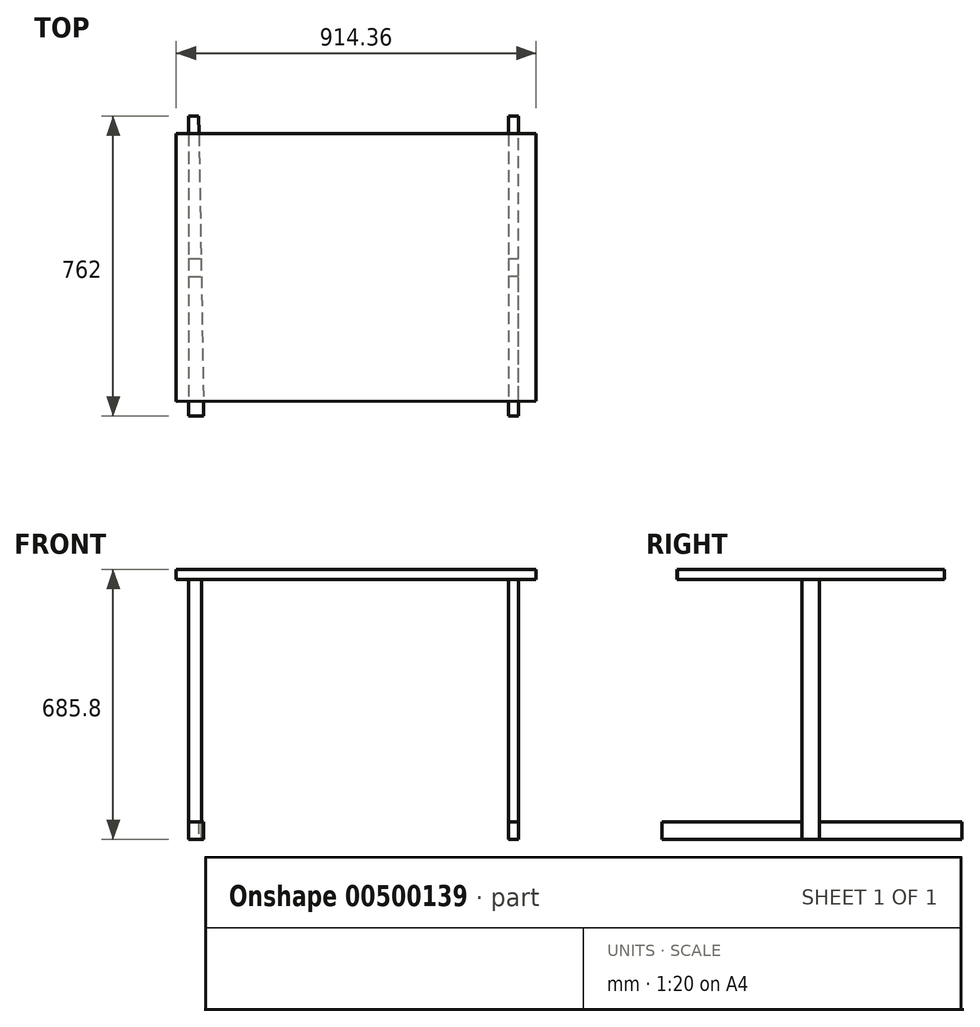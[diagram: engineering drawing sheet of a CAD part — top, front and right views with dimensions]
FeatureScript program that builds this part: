
annotation { "Feature Type Name" : "Feature", "Feature Type Description" : "" }
export const myFeature = defineFeature(function(context is Context, id is Id, definition is map)
    precondition{}
    {
        {
            var Q0;
            Q0=qCreatedBy(makeId("Top.planeOp"),FACE);
            var sketch = newSketch(context, id + "F0", { "sketchPlane" : qUnion([Q0])});
            skLineSegment(sketch, "E0", {"start": v(-52.6, 22.06) * mm, "end": v(-52.6, -739.94) * mm});
            skLineSegment(sketch, "E1", {"start": v(-52.6, -739.94) * mm, "end": v(-14.5, -739.94) * mm});
            skLineSegment(sketch, "E2", {"start": v(-52.6, 22.06) * mm, "end": v(-27.2, 22.06) * mm});
            skLineSegment(sketch, "E3", {"start": v(-27.2, 22.06) * mm, "end": v(-14.5, -739.94) * mm});
            skLineSegment(sketch, "E4", {"start": v(760.2, 22.06) * mm, "end": v(785.6, 22.06) * mm});
            skLineSegment(sketch, "E5", {"start": v(760.2, -739.94) * mm, "end": v(785.6, -739.94) * mm});
            skLineSegment(sketch, "E6", {"start": v(785.6, -739.94) * mm, "end": v(785.6, 22.06) * mm});
            skLineSegment(sketch, "E7", {"start": v(760.2, 22.06) * mm, "end": v(760.2, -739.94) * mm});
            skLineSegment(sketch, "E8", {"start": v(-52.6, -385) * mm, "end": v(-20.42, -385) * mm});
            skLineSegment(sketch, "E9", {"start": v(-52.6, -339.89) * mm, "end": v(-21.17, -339.89) * mm});
            skLineSegment(sketch, "E10", {"start": v(760.2, -384.34) * mm, "end": v(785.6, -384.34) * mm});
            skLineSegment(sketch, "E11", {"start": v(760.2, -339.89) * mm, "end": v(785.6, -339.89) * mm});
            skSolve(sketch);
        }
        {
            var Q0;
            {var subQ0=sQuery(id+"F0.wireOp",EDGE,"E1");Q0=makeQuery(id+"F0.imprint","IMPRINT",FACE,{"disambiguationData":[TD([[makeQuery(id+"F0.imprint","IMPRINT",EDGE,{"derivedFrom":subQ0}),1.0]])]});}
            var Q1;
            {var subQ0=sQuery(id+"F0.wireOp",EDGE,"E5");Q1=makeQuery(id+"F0.imprint","IMPRINT",FACE,{"disambiguationData":[TD([[makeQuery(id+"F0.imprint","IMPRINT",EDGE,{"derivedFrom":subQ0}),1.0]])]});}
            var Q2;
            {var subQ0=sQuery(id+"F0.wireOp",EDGE,"E4");Q2=makeQuery(id+"F0.imprint","IMPRINT",FACE,{"disambiguationData":[TD([[makeQuery(id+"F0.imprint","IMPRINT",EDGE,{"derivedFrom":subQ0}),-1.0]])]});}
            var Q3;
            {var subQ0=sQuery(id+"F0.wireOp",EDGE,"E2");Q3=makeQuery(id+"F0.imprint","IMPRINT",FACE,{"disambiguationData":[TD([[makeQuery(id+"F0.imprint","IMPRINT",EDGE,{"derivedFrom":subQ0}),-1.0]])]});}
            extrude(context, id + "F1", {"entities" : qUnion([Q0, Q1, Q2, Q3]), "depth" : 44.45 * mm});
        }
        {
            var Q0;
            {var subQ0=sQuery(id+"F0.wireOp",EDGE,"E8");Q0=makeQuery(id+"F0.imprint","IMPRINT",FACE,{"disambiguationData":[TD([[makeQuery(id+"F0.imprint","IMPRINT",EDGE,{"derivedFrom":subQ0}),1.0]])]});}
            var Q1;
            {var subQ0=sQuery(id+"F0.wireOp",EDGE,"E10");Q1=makeQuery(id+"F0.imprint","IMPRINT",FACE,{"disambiguationData":[TD([[makeQuery(id+"F0.imprint","IMPRINT",EDGE,{"derivedFrom":subQ0}),1.0]])]});}
            extrude(context, id + "F2", {"entities" : qUnion([Q0, Q1]), "depth" : 660.4 * mm});
        }
        {
            var Q0;
            {var subQ0=sQuery(id+"F0.wireOp",EDGE,"E9");Q0=makeQuery(id+"F0.imprint","IMPRINT",FACE,{"disambiguationData":[TD([[makeQuery(id+"F0.imprint","IMPRINT",EDGE,{"derivedFrom":subQ0}),1.0]])]});}
            var Q1;
            {var subQ0=sQuery(id+"F0.wireOp",EDGE,"E8");Q1=makeQuery(id+"F0.imprint","IMPRINT",FACE,{"disambiguationData":[TD([[makeQuery(id+"F0.imprint","IMPRINT",EDGE,{"derivedFrom":subQ0}),-1.0]])]});}
            var Q2;
            {var subQ0=sQuery(id+"F0.wireOp",EDGE,"E11");Q2=makeQuery(id+"F0.imprint","IMPRINT",FACE,{"disambiguationData":[TD([[makeQuery(id+"F0.imprint","IMPRINT",EDGE,{"derivedFrom":subQ0}),1.0]])]});}
            var Q3;
            {var subQ0=sQuery(id+"F0.wireOp",EDGE,"E10");Q3=makeQuery(id+"F0.imprint","IMPRINT",FACE,{"disambiguationData":[TD([[makeQuery(id+"F0.imprint","IMPRINT",EDGE,{"derivedFrom":subQ0}),-1.0]])]});}
            extrude(context, id + "F3", {"entities" : qUnion([Q0, Q1, Q2, Q3]), "depth" : 44.45 * mm});
        }
        {
            var Q0;
            Q0=makeQuery(id+"F2.opExtrude","CAP_FACE",FACE,{"disambiguationData":[OSD([sQuery(id+"F0.wireOp",EDGE,"E0"),sQuery(id+"F0.wireOp",EDGE,"E3"),sQuery(id+"F0.wireOp",EDGE,"E8"),sQuery(id+"F0.wireOp",EDGE,"E9")])],"isStart":false});
            var sketch = newSketch(context, id + "F4", { "sketchPlane" : qUnion([Q0])});
            skLineSegment(sketch, "E12", {"start": v(-84.35, -385) * mm, "end": v(-84.35, -702.5) * mm});
            skLineSegment(sketch, "E13", {"start": v(-84.35, -339.89) * mm, "end": v(-84.35, -22.39) * mm});
            skLineSegment(sketch, "E14", {"start": v(829.78, -383.77) * mm, "end": v(829.78, -701.27) * mm});
            skLineSegment(sketch, "E15", {"start": v(830.01, -340.21) * mm, "end": v(830.01, -22.71) * mm});
            skLineSegment(sketch, "E16", {"start": v(830.01, -340.21) * mm, "end": v(829.78, -383.77) * mm});
            skLineSegment(sketch, "E17", {"start": v(-84.35, -339.89) * mm, "end": v(-84.35, -385) * mm});
            skLineSegment(sketch, "E18", {"start": v(-84.35, -702.5) * mm, "end": v(829.78, -701.27) * mm});
            skLineSegment(sketch, "E19", {"start": v(830.01, -22.71) * mm, "end": v(-84.35, -22.39) * mm});
            skSolve(sketch);
        }
        {
            var Q0;
            Q0=makeQuery(id+"F4.imprint","IMPRINT",FACE,{"disambiguationData":[TD([[makeQuery(id+"F4.imprint","IMPRINT",EDGE,{"derivedFrom":sQuery(id+"F4.wireOp",EDGE,"E12")}),1.0]])]});
            var Q1;
            Q1=makeQuery(id+"F4.imprint","IMPRINT",FACE,{"disambiguationData":[TD([[makeQuery(id+"F4.imprint","IMPRINT",EDGE,{"derivedFrom":makeQuery(id+"F2.opExtrude","CAP_EDGE",EDGE,{"disambiguationData":[OSD([sQuery(id+"F0.wireOp",EDGE,"E0")])],"isStart":false})}),1.0]])]});
            extrude(context, id + "F5", {"entities" : qUnion([Q0, Q1]), "operationType" : NewBodyOperationType.ADD, "depth" : 25.4 * mm});
        }
    });
